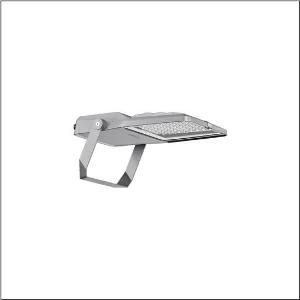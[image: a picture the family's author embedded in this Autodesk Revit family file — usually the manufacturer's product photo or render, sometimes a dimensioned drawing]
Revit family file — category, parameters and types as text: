
# Revit family: floodlight_fl_21_mini___pl61_5xa7775d2c1a_9234
name_source: partatom
category: Lighting Fixtures
units: mm (PartAtom-declared; Revit-internal decimal feet)

## family parameters
Cut with Voids When Loaded = No
Host = Face
Light Source = No
Part Type = Normal
Room Calculation Point = No
Round Connector Dimension = Use Diameter
Shared = No

## types (1)
- --- (1 x LED, 17510 lm, 142.9 W, 3000K)
    Apparent Load = 143 VA
    CIE Flux Codes = 33 65 98 100 100
    Color Rendering = 70
    Color Temperature = 3000K
    Default Elevation = 1800 mm
    Description = Floodlight FL 21 mini, floodlight, primary light control with lens, of PMMA, primary optical cover: protective disc, of toughened safety glass, transparent, light distribution: PL61, light emission: direct distribution, installation type: surface-mounted, LED, High Power LED, rated luminous flux: 17.510lm, luminous efficacy: 123lm/W, light colour: 730, colour temperature: 3000K, control: flexible luminous flux parameterisation, time-dependent luminous flux control, constant luminous flux control, overheat protection, presetting dimming logarithmic, with terminal, 6-pole, mains connection: 220..240V, AC, 50/60Hz, start of lifetime: 143W, end of service life: 151W, reduction: 63W, luminaire housing, of diecast aluminium, powder-coated, Siteco® metallic grey (DB 702S), corrosivity category C5 mid according to DIN EN ISO 12944, sealing non-destructively replaceable, mounting bracket, of steel, galvanised, powder-coated, Siteco® metallic grey (DB 702S), Smart Interface above, protection rating (complete): IP66, insulation class (complete): insulation class II (safety insulation), certification: CE, ENEC, VDE, protection symbol: D, impact resistance: IK08, permissible operating ambient temperature: -40..+40°C, permissible operating ambient temperature for outdoor applications: -40..+50°C, standard: DIN EN 12944, LABS conformity tested according to VDMA 24364:2018-05, packaging unit: 1 piece

Light Distribution: PL61
    Height = 70 mm
    Lamp = 1 x LED
    Lamp Light Flux = 17510 lm
    Lamp Power = 142.9 W
    Lamp count = 1
    Length = 485 mm
    Luminous efficacy = 123 lm/W
    Manufacturer = Siteco
    ModVariant = No
    Model = 5XA7775D2C1A
    Number of Poles = 1
    OnlyDefault = Yes
    Power Factor = 1
    Product Name = Floodlight FL 21 mini | PL61
    Product group = floodlight | pylon annexe
    ProductGroupID = 6200
    Protection Class = Protection class II
    Protection Degree = IP 66
    RLX_Detail_Level = 1
    RLX_Emergency_Light_Flux = 0 lm
    RLX_Emergency_Type = 0
    RLX_Emergency_Type_DB = No
    RlxData = <blob elided: 96241 chars, md5=90abe55f>
    Socket = socket
    Standby Power = 0 W
    System Light Flux = 17510 lm
    System Power = 143 W
    Type Comments = factory setting: luminous flux: 100 % | dim-lin: 254 | 730 mA
    Type Image = l_1006845.jpg
    URL = http://relux.com
    VarID = @adj_105037
    Voltage = 0 V
    Weight = 0.00 kg
    Width = 337 mm

## geometry (parser evidence)
native form markers: Blend x4, Sweep x12
no freeform markers — native parametric forms only
